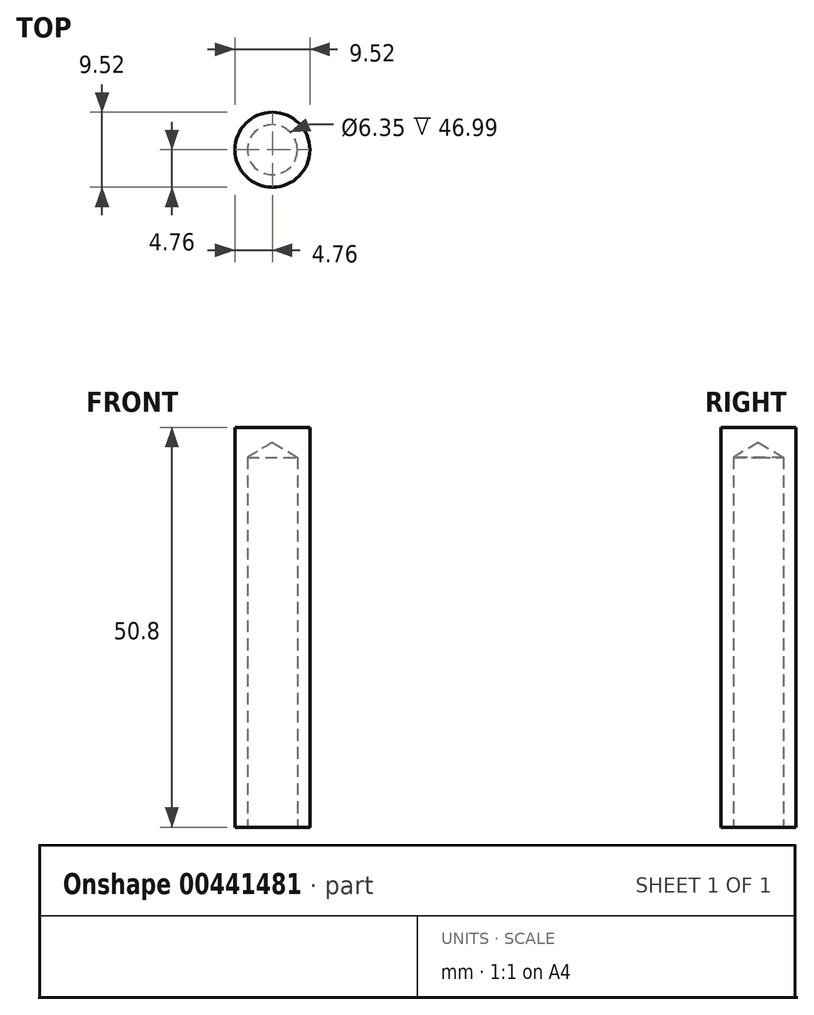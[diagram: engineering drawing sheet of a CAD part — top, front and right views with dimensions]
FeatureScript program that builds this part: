
annotation { "Feature Type Name" : "Feature", "Feature Type Description" : "" }
export const myFeature = defineFeature(function(context is Context, id is Id, definition is map)
    precondition{}
    {
        {
            var Q0;
            Q0=qCreatedBy(makeId("Front.planeOp"),FACE);
            var sketch = newSketch(context, id + "F0", { "sketchPlane" : qUnion([Q0])});
            skLineSegment(sketch, "E0.bottom", {"start": v(-4.76, -25.4) * mm, "end": v(4.76, -25.4) * mm});
            skLineSegment(sketch, "E0.top", {"start": v(-4.76, 25.4) * mm, "end": v(4.76, 25.4) * mm});
            skLineSegment(sketch, "E0.left", {"start": v(-4.76, -25.4) * mm, "end": v(-4.76, 25.4) * mm});
            skLineSegment(sketch, "E0.right", {"start": v(4.76, -25.4) * mm, "end": v(4.76, 25.4) * mm});
            skPoint(sketch, "E0.middle", {"position": v(0, 0) * mm});
            skLineSegment(sketch, "E1", {"start": v(0, -25.4) * mm, "end": v(0, 25.4) * mm});
            skSolve(sketch);
        }
        {
            var Q0;
            {var subQ0=sQuery(id+"F0.wireOp",EDGE,"E0.right");Q0=makeQuery(id+"F0.imprint","IMPRINT",FACE,{"disambiguationData":[TD([[makeQuery(id+"F0.imprint","IMPRINT",EDGE,{"derivedFrom":subQ0}),1.0]])]});}
            var Q1;
            Q1=sQuery(id+"F0.wireOp",EDGE,"E1");
            revolve(context, id + "F1", {"entities" : qUnion([Q0]), "axis" : qUnion([Q1]), "revolveType" : RevolveType.FULL});
        }
        {
            var Q0;
            Q0=makeQuery(id+"F1.opRevolve","SWEPT_FACE",FACE,{"disambiguationData":[OSD([sQuery(id+"F0.wireOp",EDGE,"E0.bottom")])]});
            var sketch = newSketch(context, id + "F2", { "sketchPlane" : qUnion([Q0])});
            skCircle(sketch, "E2", {"center": v(0, 0) * mm, "radius": 3.17 * mm});
            skSolve(sketch);
        }
        {
            var Q0;
            Q0=sQuery(id+"F2.wireOp",VERTEX,"E2.center");
            var Q1;
            Q1=makeQuery(id+"F1.opRevolve","SWEPT_BODY",BODY,{"disambiguationData":[OSD([sQuery(id+"F0.wireOp",EDGE,"E0.bottom"),sQuery(id+"F0.wireOp",EDGE,"E0.top"),sQuery(id+"F0.wireOp",EDGE,"E0.right"),sQuery(id+"F0.wireOp",EDGE,"E1")])]});
            hole(context, id + "F3", {"style" : HoleStyle.SIMPLE, "endStyle" : HoleEndStyle.BLIND, "holeDiameter" : 6.35 * mm, "holeDepth" : 47 * mm, "isTappedThrough" : true, "tappedDepth" : 12.7 * mm, "tapClearance" : 3, "startFromSketch" : true, "locations" : qUnion([Q0]), "scope" : qUnion([Q1])});
        }
    });
